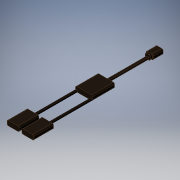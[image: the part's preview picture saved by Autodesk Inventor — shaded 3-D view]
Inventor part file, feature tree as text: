
AUTODESK INVENTOR PART (.ipt)
format: ipt  version: 2017 (Build 210142000, 142)  size: 219,136 bytes
history: native  units: in
note: dims shown in document units (in); Inventor stores cm internally (conversion verified against a paired STEP export)
features: extrude x6, sketch x1, fillet x1
ambient origin geometry x8: Origin, YZ Plane, XZ Plane, XY Plane, X Axis, Y Axis, Z Axis, Center Point
bodies: Solid1 (feature_tree)
feature tree (8):
  sketch  "Sketch1"  dims[d0=0.375in d1=0.5in d2=0.25in d3=0.125in d4=2.125in d5=0.0625in d6=0.125in d7=0.0625in d8=0.0625in d9=0.875in d10=1.125in d11=0.375in d12=2.125in d13=1.125in d14=0.1077in d15=0.125in d16=0.125in d17=2.25in d18=0.625in d19=1.0in d20=0.25in d21=2.25in d22=0.625in d23=1.0in d24=2.25in d25=0.25in d26=0.25in d27=0.0in d28=0.25in d29=0.0in d30=0.125in d31=0.0in d32=0.25in d33=0.0in d34=0.125in d35=0.0in d36=0.25in d37=0.0in d38=0.0625in]
  extrude  "Extrusion1"  Depth=0.5in
  extrude  "Extrusion2"  Depth=0.25in
  extrude  "Extrusion3"  Depth=0.125in
  extrude  "Extrusion4"  Depth=2.125in
  extrude  "Extrusion5"  Depth=0.0625in
  extrude  "Extrusion6"  Depth=0.125in
  fillet  "Fillet1"  Radius=0.0625in
